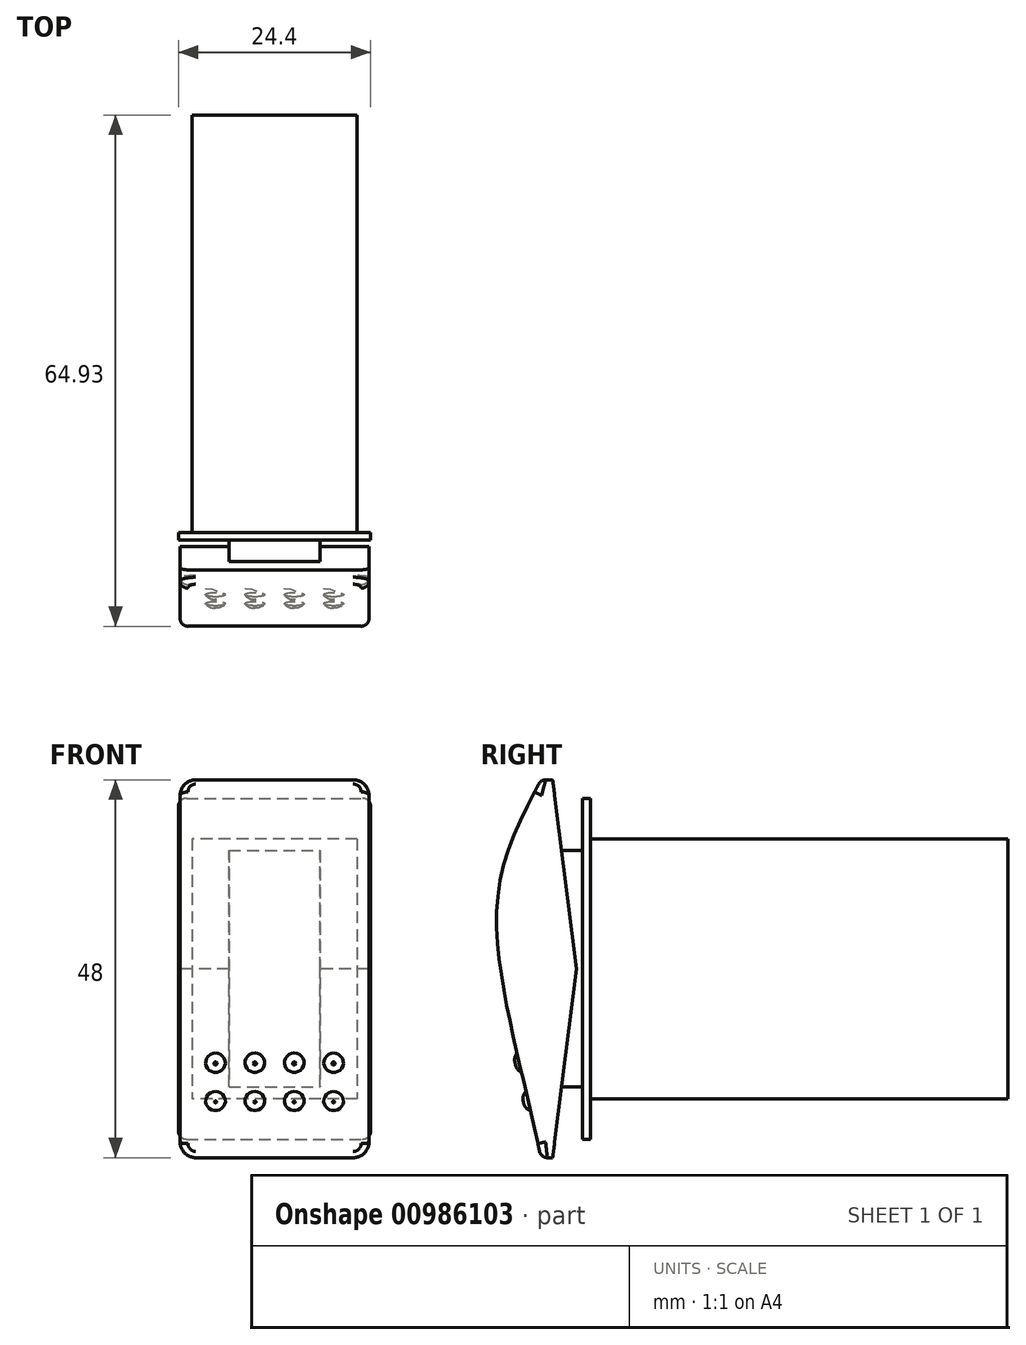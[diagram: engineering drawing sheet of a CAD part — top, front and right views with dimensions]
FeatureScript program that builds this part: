
annotation { "Feature Type Name" : "Feature", "Feature Type Description" : "" }
export const myFeature = defineFeature(function(context is Context, id is Id, definition is map)
    precondition{}
    {
        {
            var Q0;
            Q0=qCreatedBy(makeId("Front.planeOp"),FACE);
            var sketch = newSketch(context, id + "F0", { "sketchPlane" : qUnion([Q0])});
            skLineSegment(sketch, "E0.bottom", {"start": v(-12.2, 21.65) * mm, "end": v(12.2, 21.65) * mm});
            skLineSegment(sketch, "E0.top", {"start": v(-12.2, -21.65) * mm, "end": v(12.2, -21.65) * mm});
            skLineSegment(sketch, "E0.left", {"start": v(-12.2, 21.65) * mm, "end": v(-12.2, -21.65) * mm});
            skLineSegment(sketch, "E0.right", {"start": v(12.2, 21.65) * mm, "end": v(12.2, -21.65) * mm});
            skLineSegment(sketch, "E1", {"start": v(-12.2, -21.65) * mm, "end": v(12.2, 21.65) * mm, "construction": true});
            skSolve(sketch);
        }
        {
            var Q0;
            Q0 = qSketchRegion(id + "F0", true);
            extrude(context, id + "F1", {"entities" : qUnion([Q0]), "oppositeDirection" : true, "depth" : 1 * mm, "offsetDistance" : 25 * mm});
        }
        {
            var Q0;
            Q0=makeQuery(id+"F1.opExtrude","CAP_FACE",FACE,{"disambiguationData":[OSD([sQuery(id+"F0.wireOp",EDGE,"E0.bottom"),sQuery(id+"F0.wireOp",EDGE,"E0.top"),sQuery(id+"F0.wireOp",EDGE,"E0.left"),sQuery(id+"F0.wireOp",EDGE,"E0.right")])],"isStart":false});
            var sketch = newSketch(context, id + "F2", { "sketchPlane" : qUnion([Q0])});
            skLineSegment(sketch, "E2.bottom", {"start": v(-10.5, 16.5) * mm, "end": v(10.5, 16.5) * mm});
            skLineSegment(sketch, "E2.top", {"start": v(-10.5, -16.5) * mm, "end": v(10.5, -16.5) * mm});
            skLineSegment(sketch, "E2.left", {"start": v(-10.5, 16.5) * mm, "end": v(-10.5, -16.5) * mm});
            skLineSegment(sketch, "E2.right", {"start": v(10.5, 16.5) * mm, "end": v(10.5, -16.5) * mm});
            skPoint(sketch, "E3.0", {"position": v(0, 0) * mm});
            skLineSegment(sketch, "E4", {"start": v(-10.5, -16.5) * mm, "end": v(10.5, 16.5) * mm, "construction": true});
            skSolve(sketch);
        }
        {
            var Q0;
            Q0=makeQuery(id+"F2.imprint","IMPRINT",FACE,{"disambiguationData":[TD([[makeQuery(id+"F2.imprint","IMPRINT",EDGE,{"derivedFrom":sQuery(id+"F2.wireOp",EDGE,"E2.bottom")}),-1.0]])]});
            extrude(context, id + "F3", {"entities" : qUnion([Q0]), "operationType" : NewBodyOperationType.ADD, "depth" : 53 * mm, "offsetDistance" : 25 * mm});
        }
        {
            var Q0;
            Q0=makeQuery(id+"F1.opExtrude","SWEPT_EDGE",EDGE,{"disambiguationData":[OSD([sQuery(id+"F0.wireOp",EDGE,"E0.bottom"),sQuery(id+"F0.wireOp",EDGE,"E0.left")])]});
            var Q1;
            Q1=makeQuery(id+"F1.opExtrude","SWEPT_EDGE",EDGE,{"disambiguationData":[OSD([sQuery(id+"F0.wireOp",EDGE,"E0.bottom"),sQuery(id+"F0.wireOp",EDGE,"E0.right")])]});
            var Q2;
            Q2=makeQuery(id+"F1.opExtrude","SWEPT_EDGE",EDGE,{"disambiguationData":[OSD([sQuery(id+"F0.wireOp",EDGE,"E0.top"),sQuery(id+"F0.wireOp",EDGE,"E0.right")])]});
            var Q3;
            Q3=makeQuery(id+"F1.opExtrude","SWEPT_EDGE",EDGE,{"disambiguationData":[OSD([sQuery(id+"F0.wireOp",EDGE,"E0.top"),sQuery(id+"F0.wireOp",EDGE,"E0.left")])]});
            fillet(context, id + "F4", {"entities" : qUnion([Q0, Q1, Q2, Q3]), "radius" : 1 * mm, "tangentPropagation" : true, "allowEdgeOverflow" : false});
        }
        {
            var Q0;
            Q0=qCreatedBy(makeId("Right.planeOp"),FACE);
            var sketch = newSketch(context, id + "F5", { "sketchPlane" : qUnion([Q0])});
            skLineSegment(sketch, "E5", {"start": v(-5.3, -24) * mm, "end": v(-3.8, -24) * mm});
            skLineSegment(sketch, "E6", {"start": v(-3.8, -24) * mm, "end": v(-0.8, 0) * mm});
            skLineSegment(sketch, "E7", {"start": v(-0.8, 0) * mm, "end": v(-3.8, 24) * mm});
            skLineSegment(sketch, "E8", {"start": v(-3.8, 24) * mm, "end": v(-5.3, 24) * mm});
            skLineSegment(sketch, "E9", {"start": v(-3.8, 24) * mm, "end": v(-3.8, -24) * mm, "construction": true});
            skFitSpline(sketch, "E10", {"points": [v(-5.3, -24) * mm, v(-10.8, 9) * mm, v(-5.3, 24) * mm], "startDerivative": vector(-13.06, 63.35) * mm, "endDerivative": vector(15.32, 30.21) * mm});
            skSolve(sketch);
        }
        {
            var Q0;
            Q0=makeQuery(id+"F5.imprint","IMPRINT",FACE,{"disambiguationData":[TD([[makeQuery(id+"F5.imprint","IMPRINT",EDGE,{"derivedFrom":sQuery(id+"F5.wireOp",EDGE,"E5")}),1.0]])]});
            extrude(context, id + "F6", {"entities" : qUnion([Q0]), "depth" : 24 * mm, "offsetDistance" : 25 * mm, "symmetric" : true});
        }
        {
            var Q0;
            Q0=makeQuery(id+"F6.opExtrude","CAP_EDGE",EDGE,{"disambiguationData":[OSD([sQuery(id+"F5.wireOp",EDGE,"E8")])],"isStart":false});
            var Q1;
            Q1=makeQuery(id+"F6.opExtrude","CAP_EDGE",EDGE,{"disambiguationData":[OSD([sQuery(id+"F5.wireOp",EDGE,"E8")])],"isStart":true});
            var Q2;
            Q2=makeQuery(id+"F6.opExtrude","CAP_EDGE",EDGE,{"disambiguationData":[OSD([sQuery(id+"F5.wireOp",EDGE,"E5")])],"isStart":false});
            var Q3;
            Q3=makeQuery(id+"F6.opExtrude","CAP_EDGE",EDGE,{"disambiguationData":[OSD([sQuery(id+"F5.wireOp",EDGE,"E5")])],"isStart":true});
            fillet(context, id + "F7", {"entities" : qUnion([Q0, Q1, Q2, Q3]), "radius" : 2 * mm, "tangentPropagation" : true, "allowEdgeOverflow" : false});
        }
        {
            var Q0;
            Q0=makeQuery(id+"F6.opExtrude","CAP_EDGE",EDGE,{"disambiguationData":[OSD([sQuery(id+"F5.wireOp",EDGE,"E10")])],"isStart":true});
            fillet(context, id + "F8", {"entities" : qUnion([Q0]), "radius" : 1 * mm, "tangentPropagation" : true, "allowEdgeOverflow" : false});
        }
        {
            var Q0;
            Q0=makeQuery(id+"F1.opExtrude","CAP_FACE",FACE,{"disambiguationData":[OSD([sQuery(id+"F0.wireOp",EDGE,"E0.bottom"),sQuery(id+"F0.wireOp",EDGE,"E0.top"),sQuery(id+"F0.wireOp",EDGE,"E0.left"),sQuery(id+"F0.wireOp",EDGE,"E0.right")])],"isStart":true});
            var sketch = newSketch(context, id + "F9", { "sketchPlane" : qUnion([Q0])});
            skLineSegment(sketch, "E11.bottom", {"start": v(-5.79, 15.01) * mm, "end": v(5.79, 15.01) * mm});
            skLineSegment(sketch, "E11.top", {"start": v(-5.79, -15.01) * mm, "end": v(5.79, -15.01) * mm});
            skLineSegment(sketch, "E11.left", {"start": v(-5.79, 15.01) * mm, "end": v(-5.79, -15.01) * mm});
            skLineSegment(sketch, "E11.right", {"start": v(5.79, 15.01) * mm, "end": v(5.79, -15.01) * mm});
            skLineSegment(sketch, "E12", {"start": v(-5.79, -15.01) * mm, "end": v(5.79, 15.01) * mm, "construction": true});
            skSolve(sketch);
        }
        {
            var Q0;
            Q0=makeQuery(id+"F9.imprint","IMPRINT",FACE,{"disambiguationData":[TD([[makeQuery(id+"F9.imprint","IMPRINT",EDGE,{"derivedFrom":sQuery(id+"F9.wireOp",EDGE,"E11.bottom")}),-1.0]])]});
            extrude(context, id + "F10", {"entities" : qUnion([Q0]), "operationType" : NewBodyOperationType.ADD, "depth" : 3 * mm, "offsetDistance" : 25 * mm});
        }
        {
            var Q0;
            {var subQ0=sQuery(id+"F5.wireOp",EDGE,"E10");Q0=makeQuery(id+"F8.opFillet","BLEND_EDGE",EDGE,{"blendedFrom":[makeQuery(id+"F6.opExtrude","CAP_EDGE",EDGE,{"disambiguationData":[OSD([subQ0])],"isStart":false}),makeQuery(id+"F6.opExtrude","SWEPT_FACE",FACE,{"disambiguationData":[OSD([subQ0])]})],"blendedInto":[makeQuery(id+"F6.opExtrude","SWEPT_FACE",FACE,{"disambiguationData":[OSD([subQ0])]})]});}
            cPoint(context, id + "F11", {"entities" : qUnion([Q0]), "parameter" : 0.5});
        }
        {
            var Q0;
            {var subQ0=sQuery(id+"F5.wireOp",EDGE,"E10");Q0=makeQuery(id+"F8.opFillet","BLEND_EDGE",EDGE,{"blendedFrom":[makeQuery(id+"F6.opExtrude","CAP_EDGE",EDGE,{"disambiguationData":[OSD([subQ0])],"isStart":true}),makeQuery(id+"F6.opExtrude","SWEPT_FACE",FACE,{"disambiguationData":[OSD([subQ0])]})],"blendedInto":[makeQuery(id+"F6.opExtrude","SWEPT_FACE",FACE,{"disambiguationData":[OSD([subQ0])]})]});}
            cPoint(context, id + "F12", {"entities" : qUnion([Q0]), "parameter" : 0.5});
        }
        {
            var Q0;
            {var subQ0=sQuery(id+"F5.wireOp",EDGE,"E10");var subQ1=makeQuery(id+"F6.opExtrude","SWEPT_FACE",FACE,{"disambiguationData":[OSD([subQ0])]});var subQ2=sQuery(id+"F5.wireOp",EDGE,"E5");Q0=makeQuery(id+"F8.opFillet","BLEND_VERTEX",VERTEX,{"blendedFrom":[makeQuery(id+"F6.opExtrude","SWEPT_EDGE",EDGE,{"disambiguationData":[OSD([subQ2,subQ0])]}),makeQuery(id+"F7.opFillet","BLEND_EDGE",EDGE,{"blendedFrom":[makeQuery(id+"F6.opExtrude","CAP_EDGE",EDGE,{"disambiguationData":[OSD([subQ2])],"isStart":false}),subQ1],"blendedInto":[subQ1]}),subQ1],"blendedInto":[subQ1]});}
            var Q1;
            Q1 = qCreatedBy(id + "F11" ,VERTEX);
            var Q2;
            Q2 = qCreatedBy(id + "F12" ,VERTEX);
            cPlane(context, id + "F13", {"entities" : qUnion([Q0, Q1, Q2]), "cplaneType" : CPlaneType.THREE_POINT, "offset" : 25 * mm, "width" : 150 * mm, "height" : 150 * mm});
        }
        {
            var Q0;
            Q0=qCreatedBy(id+"F13.planeOp",FACE);
            var sketch = newSketch(context, id + "F14", { "sketchPlane" : qUnion([Q0])});
            skCircle(sketch, "E13", {"center": v(2.5, -15) * mm, "radius": 1.25 * mm});
            skCircle(sketch, "E14", {"center": v(7.5, -15) * mm, "radius": 1.25 * mm});
            skCircle(sketch, "E15", {"center": v(-2.5, -15) * mm, "radius": 1.25 * mm});
            skCircle(sketch, "E16", {"center": v(-7.5, -15) * mm, "radius": 1.25 * mm});
            skCircle(sketch, "E17", {"center": v(-7.5, -10) * mm, "radius": 1.25 * mm});
            skCircle(sketch, "E18", {"center": v(-2.5, -10) * mm, "radius": 1.25 * mm});
            skCircle(sketch, "E19", {"center": v(2.5, -10) * mm, "radius": 1.25 * mm});
            skCircle(sketch, "E20", {"center": v(7.5, -10) * mm, "radius": 1.25 * mm});
            skLineSegment(sketch, "E21", {"start": v(2.5, -15) * mm, "end": v(7.5, -15) * mm, "construction": true});
            skLineSegment(sketch, "E22", {"start": v(7.5, -15) * mm, "end": v(7.5, -10) * mm, "construction": true});
            skLineSegment(sketch, "E23", {"start": v(7.5, -10) * mm, "end": v(2.5, -10) * mm, "construction": true});
            skLineSegment(sketch, "E24", {"start": v(2.5, -15) * mm, "end": v(-2.5, -15) * mm, "construction": true});
            skLineSegment(sketch, "E25", {"start": v(-2.5, -15) * mm, "end": v(-7.5, -15) * mm, "construction": true});
            skLineSegment(sketch, "E26", {"start": v(-7.5, -15) * mm, "end": v(-7.5, -10) * mm, "construction": true});
            skLineSegment(sketch, "E27", {"start": v(-7.5, -10) * mm, "end": v(-2.5, -10) * mm, "construction": true});
            skLineSegment(sketch, "E28", {"start": v(-2.5, -10) * mm, "end": v(2.5, -10) * mm, "construction": true});
            skLineSegment(sketch, "E29", {"start": v(2.5, -15) * mm, "end": v(2.5, -10) * mm, "construction": true});
            skLineSegment(sketch, "E30", {"start": v(-2.5, -15) * mm, "end": v(-2.5, -10) * mm, "construction": true});
            skSolve(sketch);
        }
        {
            var Q0;
            Q0=makeQuery(id+"F14.imprint","IMPRINT",FACE,{"disambiguationData":[TD([[makeQuery(id+"F14.imprint","IMPRINT",EDGE,{"derivedFrom":sQuery(id+"F14.wireOp",EDGE,"E13")}),1.0]])]});
            var Q1;
            Q1=makeQuery(id+"F14.imprint","IMPRINT",FACE,{"disambiguationData":[TD([[makeQuery(id+"F14.imprint","IMPRINT",EDGE,{"derivedFrom":sQuery(id+"F14.wireOp",EDGE,"E14")}),1.0]])]});
            var Q2;
            Q2=makeQuery(id+"F14.imprint","IMPRINT",FACE,{"disambiguationData":[TD([[makeQuery(id+"F14.imprint","IMPRINT",EDGE,{"derivedFrom":sQuery(id+"F14.wireOp",EDGE,"E20")}),1.0]])]});
            var Q3;
            Q3=makeQuery(id+"F14.imprint","IMPRINT",FACE,{"disambiguationData":[TD([[makeQuery(id+"F14.imprint","IMPRINT",EDGE,{"derivedFrom":sQuery(id+"F14.wireOp",EDGE,"E19")}),1.0]])]});
            var Q4;
            Q4=makeQuery(id+"F14.imprint","IMPRINT",FACE,{"disambiguationData":[TD([[makeQuery(id+"F14.imprint","IMPRINT",EDGE,{"derivedFrom":sQuery(id+"F14.wireOp",EDGE,"E18")}),1.0]])]});
            var Q5;
            Q5=makeQuery(id+"F14.imprint","IMPRINT",FACE,{"disambiguationData":[TD([[makeQuery(id+"F14.imprint","IMPRINT",EDGE,{"derivedFrom":sQuery(id+"F14.wireOp",EDGE,"E17")}),1.0]])]});
            var Q6;
            Q6=makeQuery(id+"F14.imprint","IMPRINT",FACE,{"disambiguationData":[TD([[makeQuery(id+"F14.imprint","IMPRINT",EDGE,{"derivedFrom":sQuery(id+"F14.wireOp",EDGE,"E15")}),1.0]])]});
            var Q7;
            Q7=makeQuery(id+"F14.imprint","IMPRINT",FACE,{"disambiguationData":[TD([[makeQuery(id+"F14.imprint","IMPRINT",EDGE,{"derivedFrom":sQuery(id+"F14.wireOp",EDGE,"E16")}),1.0]])]});
            extrude(context, id + "F15", {"entities" : qUnion([Q0, Q1, Q2, Q3, Q4, Q5, Q6, Q7]), "operationType" : NewBodyOperationType.ADD, "oppositeDirection" : true, "depth" : 0.7 * mm, "offsetDistance" : 25 * mm});
        }
        {
            var Q0;
            Q0=makeQuery(id+"F15.opExtrude","CAP_EDGE",EDGE,{"disambiguationData":[OSD([sQuery(id+"F14.wireOp",EDGE,"E13")])],"isStart":false});
            var Q1;
            Q1=makeQuery(id+"F15.opExtrude","CAP_EDGE",EDGE,{"disambiguationData":[OSD([sQuery(id+"F14.wireOp",EDGE,"E14")])],"isStart":false});
            var Q2;
            Q2=makeQuery(id+"F15.opExtrude","CAP_EDGE",EDGE,{"disambiguationData":[OSD([sQuery(id+"F14.wireOp",EDGE,"E20")])],"isStart":false});
            var Q3;
            Q3=makeQuery(id+"F15.opExtrude","CAP_EDGE",EDGE,{"disambiguationData":[OSD([sQuery(id+"F14.wireOp",EDGE,"E19")])],"isStart":false});
            var Q4;
            Q4=makeQuery(id+"F15.opExtrude","CAP_EDGE",EDGE,{"disambiguationData":[OSD([sQuery(id+"F14.wireOp",EDGE,"E18")])],"isStart":false});
            var Q5;
            Q5=makeQuery(id+"F15.opExtrude","CAP_EDGE",EDGE,{"disambiguationData":[OSD([sQuery(id+"F14.wireOp",EDGE,"E17")])],"isStart":false});
            var Q6;
            Q6=makeQuery(id+"F15.opExtrude","CAP_EDGE",EDGE,{"disambiguationData":[OSD([sQuery(id+"F14.wireOp",EDGE,"E16")])],"isStart":false});
            var Q7;
            Q7=makeQuery(id+"F15.opExtrude","CAP_EDGE",EDGE,{"disambiguationData":[OSD([sQuery(id+"F14.wireOp",EDGE,"E15")])],"isStart":false});
            fillet(context, id + "F16", {"entities" : qUnion([Q0, Q1, Q2, Q3, Q4, Q5, Q6, Q7]), "radius" : 1.3 * mm, "tangentPropagation" : true, "allowEdgeOverflow" : false});
        }
    });
